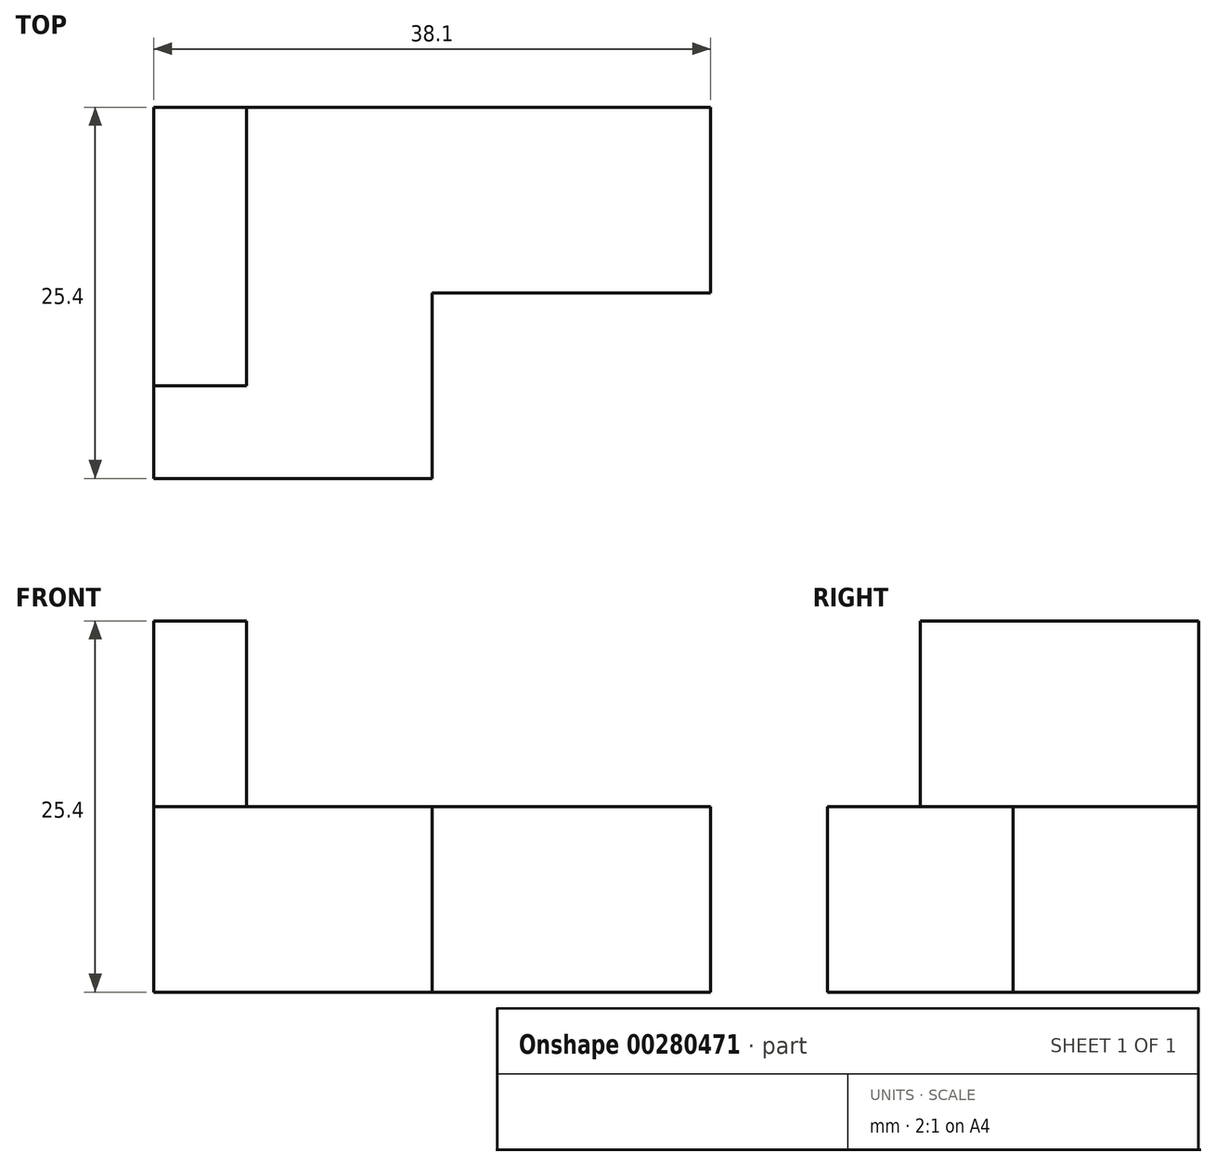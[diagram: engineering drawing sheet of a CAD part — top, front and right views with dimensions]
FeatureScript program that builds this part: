
annotation { "Feature Type Name" : "Feature", "Feature Type Description" : "" }
export const myFeature = defineFeature(function(context is Context, id is Id, definition is map)
    precondition{}
    {
        {
            var Q0;
            Q0=qCreatedBy(makeId("Front.planeOp"),FACE);
            var sketch = newSketch(context, id + "F0", { "sketchPlane" : qUnion([Q0])});
            skLineSegment(sketch, "E0", {"start": v(0, 0) * mm, "end": v(38.1, 0) * mm});
            skLineSegment(sketch, "E1", {"start": v(38.1, 0) * mm, "end": v(38.1, 12.7) * mm});
            skLineSegment(sketch, "E2", {"start": v(38.1, 12.7) * mm, "end": v(0, 12.7) * mm});
            skLineSegment(sketch, "E3", {"start": v(0, 12.7) * mm, "end": v(0, 0) * mm});
            skLineSegment(sketch, "E4", {"start": v(0, 12.7) * mm, "end": v(0, 25.4) * mm});
            skLineSegment(sketch, "E5", {"start": v(0, 25.4) * mm, "end": v(6.35, 25.4) * mm});
            skLineSegment(sketch, "E6", {"start": v(6.35, 25.4) * mm, "end": v(6.35, 12.7) * mm});
            skLineSegment(sketch, "E7", {"start": v(6.35, 12.7) * mm, "end": v(0, 12.7) * mm});
            skSolve(sketch);
        }
        {
            var Q0;
            Q0=makeQuery(id+"F0.imprint","IMPRINT",FACE,{"disambiguationData":[TD([[makeQuery(id+"F0.imprint","IMPRINT",EDGE,{"derivedFrom":sQuery(id+"F0.wireOp",EDGE,"E4")}),-1.0]])]});
            extrude(context, id + "F1", {"entities" : qUnion([Q0]), "depth" : 19.05 * mm});
        }
        {
            var Q0;
            Q0=makeQuery(id+"F0.imprint","IMPRINT",FACE,{"disambiguationData":[TD([[makeQuery(id+"F0.imprint","IMPRINT",EDGE,{"derivedFrom":sQuery(id+"F0.wireOp",EDGE,"E0")}),1.0]])]});
            extrude(context, id + "F2", {"entities" : qUnion([Q0]), "operationType" : NewBodyOperationType.ADD, "depth" : 25.4 * mm});
        }
        {
            var Q0;
            Q0=makeQuery(id+"F2.opExtrude","SWEPT_FACE",FACE,{"disambiguationData":[OSD([sQuery(id+"F0.wireOp",EDGE,"E1")])]});
            var sketch = newSketch(context, id + "F3", { "sketchPlane" : qUnion([Q0])});
            skLineSegment(sketch, "E8", {"start": v(-12.7, 0) * mm, "end": v(-12.7, 12.7) * mm});
            skLineSegment(sketch, "E9", {"start": v(-12.7, 12.7) * mm, "end": v(-25.4, 12.7) * mm});
            skLineSegment(sketch, "E10", {"start": v(-25.4, 12.7) * mm, "end": v(-25.4, 0) * mm});
            skLineSegment(sketch, "E11", {"start": v(-25.4, 0) * mm, "end": v(-12.7, 0) * mm});
            skSolve(sketch);
        }
        {
            var Q0;
            Q0=makeQuery(id+"F3.imprint","IMPRINT",FACE,{"disambiguationData":[TD([[makeQuery(id+"F3.imprint","IMPRINT",EDGE,{"derivedFrom":sQuery(id+"F3.wireOp",EDGE,"E8")}),1.0]])]});
            extrude(context, id + "F4", {"entities" : qUnion([Q0]), "operationType" : NewBodyOperationType.REMOVE, "oppositeDirection" : true, "depth" : 19.05 * mm});
        }
    });
